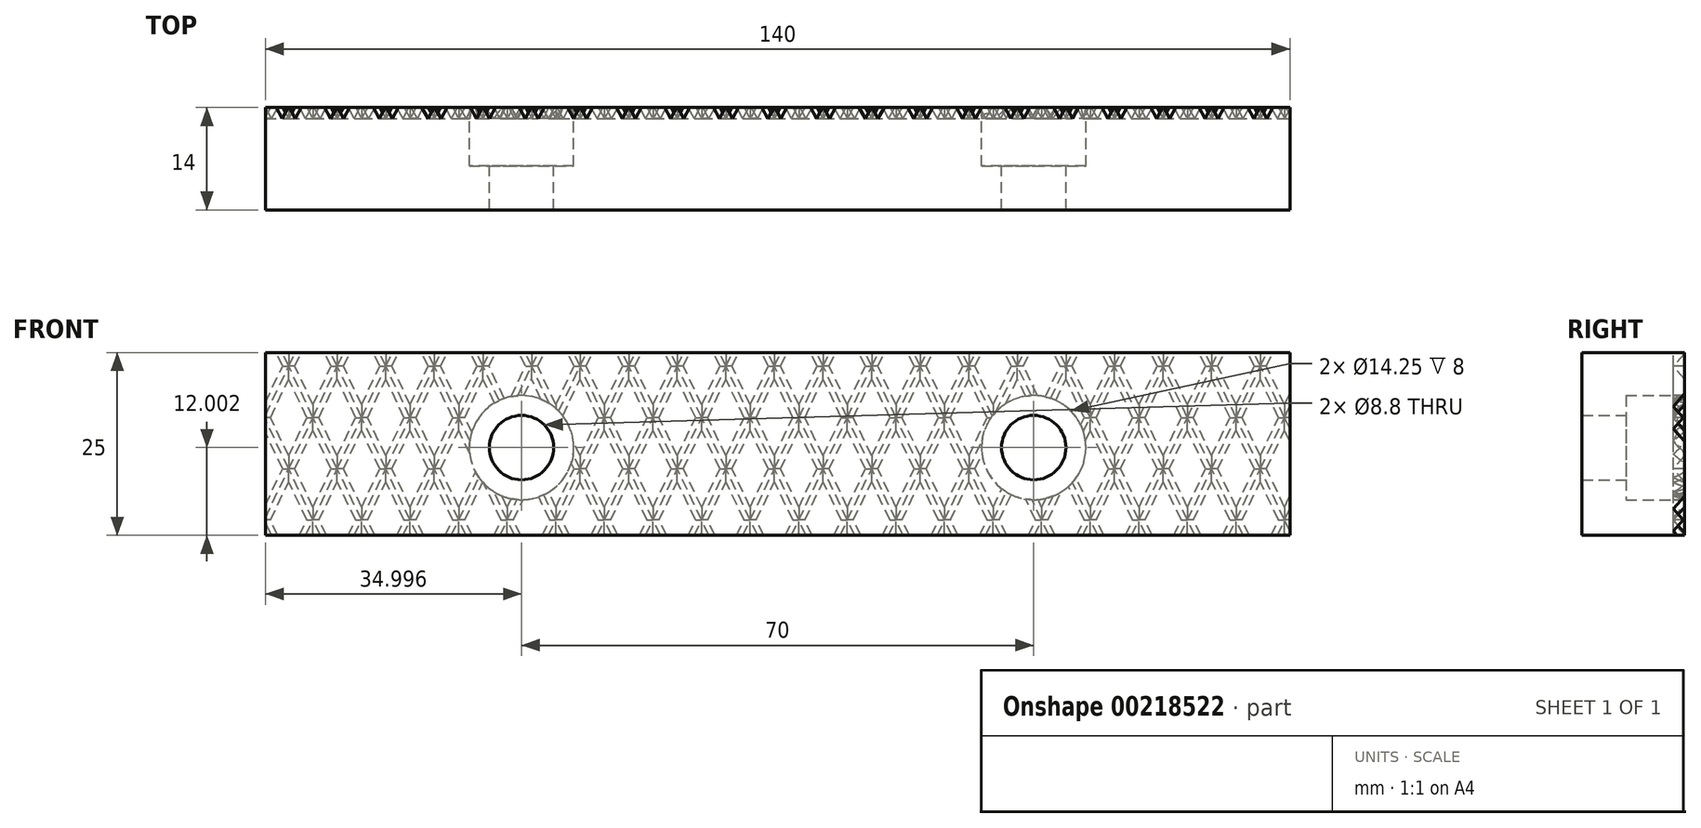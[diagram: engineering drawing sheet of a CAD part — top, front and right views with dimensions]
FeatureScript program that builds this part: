
annotation { "Feature Type Name" : "Feature", "Feature Type Description" : "" }
export const myFeature = defineFeature(function(context is Context, id is Id, definition is map)
    precondition{}
    {
        {
            var Q0;
            Q0=qCreatedBy(makeId("Front.planeOp"),FACE);
            var sketch = newSketch(context, id + "F0", { "sketchPlane" : qUnion([Q0])});
            skLineSegment(sketch, "E0.bottom", {"start": v(-70.74, 11.15) * mm, "end": v(69.26, 11.15) * mm});
            skLineSegment(sketch, "E0.top", {"start": v(-70.74, -13.85) * mm, "end": v(69.26, -13.85) * mm});
            skLineSegment(sketch, "E0.left", {"start": v(-70.74, 11.15) * mm, "end": v(-70.74, -13.85) * mm});
            skLineSegment(sketch, "E0.right", {"start": v(69.26, 11.15) * mm, "end": v(69.26, -13.85) * mm});
            skLineSegment(sketch, "E1", {"start": v(-70.74, -13.85) * mm, "end": v(-35.74, -13.85) * mm});
            skLineSegment(sketch, "E2", {"start": v(-35.74, -13.85) * mm, "end": v(-35.74, -1.85) * mm});
            skLineSegment(sketch, "E3", {"start": v(-35.74, -1.85) * mm, "end": v(34.26, -1.85) * mm});
            skSolve(sketch);
        }
        {
            var Q0;
            Q0=makeQuery(id+"F0.imprint","IMPRINT",FACE,{"disambiguationData":[TD([[makeQuery(id+"F0.imprint","IMPRINT",EDGE,{"derivedFrom":sQuery(id+"F0.wireOp",EDGE,"E0.bottom")}),-1.0]])]});
            extrude(context, id + "F1", {"entities" : qUnion([Q0]), "depth" : 14 * mm});
        }
        {
            var Q0;
            Q0=sQuery(id+"F0.wireOp",VERTEX,"E3.start");
            var Q1;
            Q1=sQuery(id+"F0.wireOp",VERTEX,"E3.end");
            var Q2;
            Q2=makeQuery(id+"F1.opExtrude","SWEPT_BODY",BODY,{"disambiguationData":[OSD([sQuery(id+"F0.wireOp",EDGE,"E0.bottom"),sQuery(id+"F0.wireOp",EDGE,"E0.top"),sQuery(id+"F0.wireOp",EDGE,"E0.left"),sQuery(id+"F0.wireOp",EDGE,"E0.right"),sQuery(id+"F0.wireOp",EDGE,"E1")])]});
            hole(context, id + "F2", {"style" : HoleStyle.C_BORE, "endStyle" : HoleEndStyle.THROUGH, "oppositeDirection" : true, "standardTappedOrClearance" : lookupTablePath({ "standard" : "ISO", "fit" : "Normal", "size" : "M8", "type" : "Clearance" }), "standardBlindInLast" : lookupTablePath({ "fit" : "Standard", "standard" : "ISO", "size" : "M8", "type" : "Clearance" }), "holeDiameter" : 8.8 * mm, "cBoreDiameter" : 14.25 * mm, "cBoreDepth" : 8 * mm, "isTappedThrough" : true, "tappedDepth" : 12 * mm, "tapClearance" : 3, "locations" : qUnion([Q0, Q1]), "scope" : qUnion([Q2])});
        }
        {
            var Q0;
            Q0=sQuery(id+"F0.wireOp",EDGE,"E0.top");
            cPoint(context, id + "F3", {"entities" : qUnion([Q0]), "parameter" : 0.5});
        }
        {
            var Q0;
            Q0=makeQuery(id+"F1.opExtrude","SWEPT_EDGE",EDGE,{"disambiguationData":[OSD([sQuery(id+"F0.wireOp",EDGE,"E0.bottom"),sQuery(id+"F0.wireOp",EDGE,"E0.right")])]});
            var Q1;
            Q1 = qCreatedBy(id + "F3" ,VERTEX);
            cPlane(context, id + "F4", {"entities" : qUnion([Q0, Q1]), "cplaneType" : CPlaneType.LINE_ANGLE, "offset" : 25 * mm, "angle" : 45 * degree, "width" : 150 * mm, "height" : 150 * mm});
        }
        {
            var Q0;
            Q0=qCreatedBy(id+"F4.planeOp",FACE);
            var sketch = newSketch(context, id + "F5", { "sketchPlane" : qUnion([Q0])});
            skLineSegment(sketch, "E4", {"start": v(0, 0) * mm, "end": v(126.29, 0) * mm});
            skLineSegment(sketch, "E5", {"start": v(0, 0) * mm, "end": v(-124.5, 0) * mm});
            skLineSegment(sketch, "E6", {"start": v(67.71, 0) * mm, "end": v(66.21, 0) * mm});
            skLineSegment(sketch, "E7", {"start": v(66.96, -1.5) * mm, "end": v(66.21, 0) * mm});
            skLineSegment(sketch, "E8", {"start": v(66.96, -1.5) * mm, "end": v(67.71, 0) * mm});
            skLineSegment(sketch, "E9.1.0.0", {"start": v(60.96, -1.5) * mm, "end": v(60.21, 0) * mm});
            skLineSegment(sketch, "E9.2.0.0", {"start": v(54.96, -1.5) * mm, "end": v(54.21, 0) * mm});
            skLineSegment(sketch, "E9.3.0.0", {"start": v(48.96, -1.5) * mm, "end": v(48.21, 0) * mm});
            skLineSegment(sketch, "E9.4.0.0", {"start": v(42.96, -1.5) * mm, "end": v(42.21, 0) * mm});
            skLineSegment(sketch, "E9.5.0.0", {"start": v(36.96, -1.5) * mm, "end": v(36.21, 0) * mm});
            skLineSegment(sketch, "E9.6.0.0", {"start": v(30.96, -1.5) * mm, "end": v(30.21, 0) * mm});
            skLineSegment(sketch, "E9.7.0.0", {"start": v(24.96, -1.5) * mm, "end": v(24.21, 0) * mm});
            skLineSegment(sketch, "E9.8.0.0", {"start": v(18.96, -1.5) * mm, "end": v(18.21, 0) * mm});
            skLineSegment(sketch, "E9.9.0.0", {"start": v(12.96, -1.5) * mm, "end": v(12.21, 0) * mm});
            skLineSegment(sketch, "E9.10.0.0", {"start": v(6.96, -1.5) * mm, "end": v(6.21, 0) * mm});
            skLineSegment(sketch, "E9.11.0.0", {"start": v(0.96, -1.5) * mm, "end": v(0.21, 0) * mm});
            skLineSegment(sketch, "E9.12.0.0", {"start": v(-5.04, -1.5) * mm, "end": v(-5.79, 0) * mm});
            skLineSegment(sketch, "E9.13.0.0", {"start": v(-11.04, -1.5) * mm, "end": v(-11.79, 0) * mm});
            skLineSegment(sketch, "E9.14.0.0", {"start": v(-17.04, -1.5) * mm, "end": v(-17.79, 0) * mm});
            skLineSegment(sketch, "E9.15.0.0", {"start": v(-23.04, -1.5) * mm, "end": v(-23.79, 0) * mm});
            skLineSegment(sketch, "E9.16.0.0", {"start": v(-29.04, -1.5) * mm, "end": v(-29.79, 0) * mm});
            skLineSegment(sketch, "E9.17.0.0", {"start": v(-35.04, -1.5) * mm, "end": v(-35.79, 0) * mm});
            skLineSegment(sketch, "E9.18.0.0", {"start": v(-41.04, -1.5) * mm, "end": v(-41.79, 0) * mm});
            skLineSegment(sketch, "E9.19.0.0", {"start": v(-47.04, -1.5) * mm, "end": v(-47.79, 0) * mm});
            skLineSegment(sketch, "E9.20.0.0", {"start": v(-53.04, -1.5) * mm, "end": v(-53.79, 0) * mm});
            skLineSegment(sketch, "E9.21.0.0", {"start": v(-59.04, -1.5) * mm, "end": v(-59.79, 0) * mm});
            skLineSegment(sketch, "E9.22.0.0", {"start": v(-65.04, -1.5) * mm, "end": v(-65.79, 0) * mm});
            skLineSegment(sketch, "E9.23.0.0", {"start": v(-71.04, -1.5) * mm, "end": v(-71.79, 0) * mm});
            skLineSegment(sketch, "E9.24.0.0", {"start": v(-77.04, -1.5) * mm, "end": v(-77.79, 0) * mm});
            skLineSegment(sketch, "E9.25.0.0", {"start": v(-83.04, -1.5) * mm, "end": v(-83.79, 0) * mm});
            skLineSegment(sketch, "E9.26.0.0", {"start": v(-89.04, -1.5) * mm, "end": v(-89.79, 0) * mm});
            skLineSegment(sketch, "E9.27.0.0", {"start": v(-95.04, -1.5) * mm, "end": v(-95.79, 0) * mm});
            skLineSegment(sketch, "E9.28.0.0", {"start": v(-101.04, -1.5) * mm, "end": v(-101.79, 0) * mm});
            skLineSegment(sketch, "E9.29.0.0", {"start": v(-107.04, -1.5) * mm, "end": v(-107.79, 0) * mm});
            skLineSegment(sketch, "E9.direction1", {"start": v(66.96, -1.5) * mm, "end": v(60.96, -1.5) * mm, "construction": true});
            skLineSegment(sketch, "E10.1.0.0", {"start": v(60.96, -1.5) * mm, "end": v(61.71, 0) * mm});
            skLineSegment(sketch, "E10.2.0.0", {"start": v(54.96, -1.5) * mm, "end": v(55.71, 0) * mm});
            skLineSegment(sketch, "E10.3.0.0", {"start": v(48.96, -1.5) * mm, "end": v(49.71, 0) * mm});
            skLineSegment(sketch, "E10.4.0.0", {"start": v(42.96, -1.5) * mm, "end": v(43.71, 0) * mm});
            skLineSegment(sketch, "E10.5.0.0", {"start": v(36.96, -1.5) * mm, "end": v(37.71, 0) * mm});
            skLineSegment(sketch, "E10.6.0.0", {"start": v(30.96, -1.5) * mm, "end": v(31.71, 0) * mm});
            skLineSegment(sketch, "E10.7.0.0", {"start": v(24.96, -1.5) * mm, "end": v(25.71, 0) * mm});
            skLineSegment(sketch, "E10.8.0.0", {"start": v(18.96, -1.5) * mm, "end": v(19.71, 0) * mm});
            skLineSegment(sketch, "E10.9.0.0", {"start": v(12.96, -1.5) * mm, "end": v(13.71, 0) * mm});
            skLineSegment(sketch, "E10.10.0.0", {"start": v(6.96, -1.5) * mm, "end": v(7.71, 0) * mm});
            skLineSegment(sketch, "E10.11.0.0", {"start": v(0.96, -1.5) * mm, "end": v(1.71, 0) * mm});
            skLineSegment(sketch, "E10.12.0.0", {"start": v(-5.04, -1.5) * mm, "end": v(-4.29, 0) * mm});
            skLineSegment(sketch, "E10.13.0.0", {"start": v(-11.04, -1.5) * mm, "end": v(-10.29, 0) * mm});
            skLineSegment(sketch, "E10.14.0.0", {"start": v(-17.04, -1.5) * mm, "end": v(-16.29, 0) * mm});
            skLineSegment(sketch, "E10.15.0.0", {"start": v(-23.04, -1.5) * mm, "end": v(-22.29, 0) * mm});
            skLineSegment(sketch, "E10.16.0.0", {"start": v(-29.04, -1.5) * mm, "end": v(-28.29, 0) * mm});
            skLineSegment(sketch, "E10.17.0.0", {"start": v(-35.04, -1.5) * mm, "end": v(-34.29, 0) * mm});
            skLineSegment(sketch, "E10.18.0.0", {"start": v(-41.04, -1.5) * mm, "end": v(-40.29, 0) * mm});
            skLineSegment(sketch, "E10.19.0.0", {"start": v(-47.04, -1.5) * mm, "end": v(-46.29, 0) * mm});
            skLineSegment(sketch, "E10.20.0.0", {"start": v(-53.04, -1.5) * mm, "end": v(-52.29, 0) * mm});
            skLineSegment(sketch, "E10.21.0.0", {"start": v(-59.04, -1.5) * mm, "end": v(-58.29, 0) * mm});
            skLineSegment(sketch, "E10.22.0.0", {"start": v(-65.04, -1.5) * mm, "end": v(-64.29, 0) * mm});
            skLineSegment(sketch, "E10.23.0.0", {"start": v(-71.04, -1.5) * mm, "end": v(-70.29, 0) * mm});
            skLineSegment(sketch, "E10.24.0.0", {"start": v(-77.04, -1.5) * mm, "end": v(-76.29, 0) * mm});
            skLineSegment(sketch, "E10.25.0.0", {"start": v(-83.04, -1.5) * mm, "end": v(-82.29, 0) * mm});
            skLineSegment(sketch, "E10.26.0.0", {"start": v(-89.04, -1.5) * mm, "end": v(-88.29, 0) * mm});
            skLineSegment(sketch, "E10.27.0.0", {"start": v(-95.04, -1.5) * mm, "end": v(-94.29, 0) * mm});
            skLineSegment(sketch, "E10.28.0.0", {"start": v(-101.04, -1.5) * mm, "end": v(-100.29, 0) * mm});
            skLineSegment(sketch, "E10.29.0.0", {"start": v(-107.04, -1.5) * mm, "end": v(-106.29, 0) * mm});
            skLineSegment(sketch, "E11.1.0.0", {"start": v(61.71, 0) * mm, "end": v(60.21, 0) * mm});
            skLineSegment(sketch, "E11.2.0.0", {"start": v(55.71, 0) * mm, "end": v(54.21, 0) * mm});
            skLineSegment(sketch, "E11.3.0.0", {"start": v(49.71, 0) * mm, "end": v(48.21, 0) * mm});
            skLineSegment(sketch, "E11.4.0.0", {"start": v(43.71, 0) * mm, "end": v(42.21, 0) * mm});
            skLineSegment(sketch, "E11.5.0.0", {"start": v(37.71, 0) * mm, "end": v(36.21, 0) * mm});
            skLineSegment(sketch, "E11.6.0.0", {"start": v(31.71, 0) * mm, "end": v(30.21, 0) * mm});
            skLineSegment(sketch, "E11.7.0.0", {"start": v(25.71, 0) * mm, "end": v(24.21, 0) * mm});
            skLineSegment(sketch, "E11.8.0.0", {"start": v(19.71, 0) * mm, "end": v(18.21, 0) * mm});
            skLineSegment(sketch, "E11.9.0.0", {"start": v(13.71, 0) * mm, "end": v(12.21, 0) * mm});
            skLineSegment(sketch, "E11.10.0.0", {"start": v(7.71, 0) * mm, "end": v(6.21, 0) * mm});
            skLineSegment(sketch, "E11.11.0.0", {"start": v(1.71, 0) * mm, "end": v(0.21, 0) * mm});
            skLineSegment(sketch, "E11.12.0.0", {"start": v(-4.29, 0) * mm, "end": v(-5.79, 0) * mm});
            skLineSegment(sketch, "E11.13.0.0", {"start": v(-10.29, 0) * mm, "end": v(-11.79, 0) * mm});
            skLineSegment(sketch, "E11.14.0.0", {"start": v(-16.29, 0) * mm, "end": v(-17.79, 0) * mm});
            skLineSegment(sketch, "E11.15.0.0", {"start": v(-22.29, 0) * mm, "end": v(-23.79, 0) * mm});
            skLineSegment(sketch, "E11.16.0.0", {"start": v(-28.29, 0) * mm, "end": v(-29.79, 0) * mm});
            skLineSegment(sketch, "E11.17.0.0", {"start": v(-34.29, 0) * mm, "end": v(-35.79, 0) * mm});
            skLineSegment(sketch, "E11.18.0.0", {"start": v(-40.29, 0) * mm, "end": v(-41.79, 0) * mm});
            skLineSegment(sketch, "E11.19.0.0", {"start": v(-46.29, 0) * mm, "end": v(-47.79, 0) * mm});
            skLineSegment(sketch, "E11.20.0.0", {"start": v(-52.29, 0) * mm, "end": v(-53.79, 0) * mm});
            skLineSegment(sketch, "E11.21.0.0", {"start": v(-58.29, 0) * mm, "end": v(-59.79, 0) * mm});
            skLineSegment(sketch, "E11.22.0.0", {"start": v(-64.29, 0) * mm, "end": v(-65.79, 0) * mm});
            skLineSegment(sketch, "E11.23.0.0", {"start": v(-70.29, 0) * mm, "end": v(-71.79, 0) * mm});
            skLineSegment(sketch, "E11.24.0.0", {"start": v(-76.29, 0) * mm, "end": v(-77.79, 0) * mm});
            skLineSegment(sketch, "E11.25.0.0", {"start": v(-82.29, 0) * mm, "end": v(-83.79, 0) * mm});
            skLineSegment(sketch, "E11.26.0.0", {"start": v(-88.29, 0) * mm, "end": v(-89.79, 0) * mm});
            skLineSegment(sketch, "E11.27.0.0", {"start": v(-94.29, 0) * mm, "end": v(-95.79, 0) * mm});
            skLineSegment(sketch, "E11.28.0.0", {"start": v(-100.29, 0) * mm, "end": v(-101.79, 0) * mm});
            skLineSegment(sketch, "E11.29.0.0", {"start": v(-106.29, 0) * mm, "end": v(-107.79, 0) * mm});
            skLineSegment(sketch, "E11.direction1", {"start": v(66.21, 0) * mm, "end": v(60.21, 0) * mm, "construction": true});
            skSolve(sketch);
        }
        {
            var Q0;
            Q0 = qSketchRegion(id + "F5", true);
            extrude(context, id + "F6", {"entities" : qUnion([Q0]), "operationType" : NewBodyOperationType.REMOVE, "endBound" : BoundingType.SYMMETRIC, "oppositeDirection" : true, "depth" : 300 * mm});
        }
        {
            var Q0;
            Q0=sQuery(id+"F0.wireOp",EDGE,"E0.top");
            cPoint(context, id + "F7", {"entities" : qUnion([Q0]), "parameter" : 0.5});
        }
        {
            var Q0;
            Q0=makeQuery(id+"F1.opExtrude","SWEPT_EDGE",EDGE,{"disambiguationData":[OSD([sQuery(id+"F0.wireOp",EDGE,"E0.bottom"),sQuery(id+"F0.wireOp",EDGE,"E0.left")])]});
            var Q1;
            Q1 = qCreatedBy(id + "F7" ,VERTEX);
            cPlane(context, id + "F8", {"entities" : qUnion([Q0, Q1]), "cplaneType" : CPlaneType.LINE_ANGLE, "offset" : 25 * mm, "angle" : 135 * degree, "width" : 150 * mm, "height" : 150 * mm});
        }
        {
            var Q0;
            Q0=qCreatedBy(id+"F8.planeOp",FACE);
            var sketch = newSketch(context, id + "F9", { "sketchPlane" : qUnion([Q0])});
            skLineSegment(sketch, "E12", {"start": v(0, 0) * mm, "end": v(-89.04, 0) * mm});
            skLineSegment(sketch, "E13", {"start": v(0, 0) * mm, "end": v(96.12, 0) * mm});
            skLineSegment(sketch, "E14", {"start": v(-69.84, 0) * mm, "end": v(-68.34, 0) * mm});
            skLineSegment(sketch, "E15", {"start": v(-69.1, -1.5) * mm, "end": v(-68.34, 0) * mm});
            skLineSegment(sketch, "E16", {"start": v(-69.1, -1.5) * mm, "end": v(-69.84, 0) * mm});
            skLineSegment(sketch, "E17.1.0.0", {"start": v(-63.1, -1.5) * mm, "end": v(-63.84, 0) * mm});
            skLineSegment(sketch, "E17.2.0.0", {"start": v(-57.1, -1.5) * mm, "end": v(-57.84, 0) * mm});
            skLineSegment(sketch, "E17.3.0.0", {"start": v(-51.1, -1.5) * mm, "end": v(-51.84, 0) * mm});
            skLineSegment(sketch, "E17.4.0.0", {"start": v(-45.1, -1.5) * mm, "end": v(-45.84, 0) * mm});
            skLineSegment(sketch, "E17.5.0.0", {"start": v(-39.1, -1.5) * mm, "end": v(-39.84, 0) * mm});
            skLineSegment(sketch, "E17.6.0.0", {"start": v(-33.1, -1.5) * mm, "end": v(-33.84, 0) * mm});
            skLineSegment(sketch, "E17.7.0.0", {"start": v(-27.1, -1.5) * mm, "end": v(-27.84, 0) * mm});
            skLineSegment(sketch, "E17.8.0.0", {"start": v(-21.1, -1.5) * mm, "end": v(-21.84, 0) * mm});
            skLineSegment(sketch, "E17.9.0.0", {"start": v(-15.1, -1.5) * mm, "end": v(-15.84, 0) * mm});
            skLineSegment(sketch, "E17.10.0.0", {"start": v(-9.1, -1.5) * mm, "end": v(-9.84, 0) * mm});
            skLineSegment(sketch, "E17.11.0.0", {"start": v(-3.1, -1.5) * mm, "end": v(-3.84, 0) * mm});
            skLineSegment(sketch, "E17.12.0.0", {"start": v(2.9, -1.5) * mm, "end": v(2.16, 0) * mm});
            skLineSegment(sketch, "E17.13.0.0", {"start": v(8.9, -1.5) * mm, "end": v(8.16, 0) * mm});
            skLineSegment(sketch, "E17.14.0.0", {"start": v(14.9, -1.5) * mm, "end": v(14.16, 0) * mm});
            skLineSegment(sketch, "E17.15.0.0", {"start": v(20.9, -1.5) * mm, "end": v(20.16, 0) * mm});
            skLineSegment(sketch, "E17.16.0.0", {"start": v(26.9, -1.5) * mm, "end": v(26.16, 0) * mm});
            skLineSegment(sketch, "E17.17.0.0", {"start": v(32.9, -1.5) * mm, "end": v(32.16, 0) * mm});
            skLineSegment(sketch, "E17.18.0.0", {"start": v(38.9, -1.5) * mm, "end": v(38.16, 0) * mm});
            skLineSegment(sketch, "E17.19.0.0", {"start": v(44.9, -1.5) * mm, "end": v(44.16, 0) * mm});
            skLineSegment(sketch, "E17.20.0.0", {"start": v(50.9, -1.5) * mm, "end": v(50.16, 0) * mm});
            skLineSegment(sketch, "E17.21.0.0", {"start": v(56.9, -1.5) * mm, "end": v(56.16, 0) * mm});
            skLineSegment(sketch, "E17.22.0.0", {"start": v(62.9, -1.5) * mm, "end": v(62.16, 0) * mm});
            skLineSegment(sketch, "E17.23.0.0", {"start": v(68.9, -1.5) * mm, "end": v(68.16, 0) * mm});
            skLineSegment(sketch, "E17.24.0.0", {"start": v(74.9, -1.5) * mm, "end": v(74.16, 0) * mm});
            skLineSegment(sketch, "E17.25.0.0", {"start": v(80.9, -1.5) * mm, "end": v(80.16, 0) * mm});
            skLineSegment(sketch, "E17.26.0.0", {"start": v(86.9, -1.5) * mm, "end": v(86.16, 0) * mm});
            skLineSegment(sketch, "E17.27.0.0", {"start": v(92.9, -1.5) * mm, "end": v(92.16, 0) * mm});
            skLineSegment(sketch, "E17.28.0.0", {"start": v(98.9, -1.5) * mm, "end": v(98.16, 0) * mm});
            skLineSegment(sketch, "E17.29.0.0", {"start": v(104.9, -1.5) * mm, "end": v(104.16, 0) * mm});
            skLineSegment(sketch, "E17.direction1", {"start": v(-69.1, -1.5) * mm, "end": v(-63.1, -1.5) * mm, "construction": true});
            skLineSegment(sketch, "E18.1.0.0", {"start": v(-63.1, -1.5) * mm, "end": v(-62.34, 0) * mm});
            skLineSegment(sketch, "E18.2.0.0", {"start": v(-57.1, -1.5) * mm, "end": v(-56.34, 0) * mm});
            skLineSegment(sketch, "E18.3.0.0", {"start": v(-51.1, -1.5) * mm, "end": v(-50.34, 0) * mm});
            skLineSegment(sketch, "E18.4.0.0", {"start": v(-45.1, -1.5) * mm, "end": v(-44.34, 0) * mm});
            skLineSegment(sketch, "E18.5.0.0", {"start": v(-39.1, -1.5) * mm, "end": v(-38.34, 0) * mm});
            skLineSegment(sketch, "E18.6.0.0", {"start": v(-33.1, -1.5) * mm, "end": v(-32.34, 0) * mm});
            skLineSegment(sketch, "E18.7.0.0", {"start": v(-27.1, -1.5) * mm, "end": v(-26.34, 0) * mm});
            skLineSegment(sketch, "E18.8.0.0", {"start": v(-21.1, -1.5) * mm, "end": v(-20.34, 0) * mm});
            skLineSegment(sketch, "E18.9.0.0", {"start": v(-15.1, -1.5) * mm, "end": v(-14.34, 0) * mm});
            skLineSegment(sketch, "E18.10.0.0", {"start": v(-9.1, -1.5) * mm, "end": v(-8.34, 0) * mm});
            skLineSegment(sketch, "E18.11.0.0", {"start": v(-3.1, -1.5) * mm, "end": v(-2.34, 0) * mm});
            skLineSegment(sketch, "E18.12.0.0", {"start": v(2.9, -1.5) * mm, "end": v(3.66, 0) * mm});
            skLineSegment(sketch, "E18.13.0.0", {"start": v(8.9, -1.5) * mm, "end": v(9.66, 0) * mm});
            skLineSegment(sketch, "E18.14.0.0", {"start": v(14.9, -1.5) * mm, "end": v(15.66, 0) * mm});
            skLineSegment(sketch, "E18.15.0.0", {"start": v(20.9, -1.5) * mm, "end": v(21.66, 0) * mm});
            skLineSegment(sketch, "E18.16.0.0", {"start": v(26.9, -1.5) * mm, "end": v(27.66, 0) * mm});
            skLineSegment(sketch, "E18.17.0.0", {"start": v(32.9, -1.5) * mm, "end": v(33.66, 0) * mm});
            skLineSegment(sketch, "E18.18.0.0", {"start": v(38.9, -1.5) * mm, "end": v(39.66, 0) * mm});
            skLineSegment(sketch, "E18.19.0.0", {"start": v(44.9, -1.5) * mm, "end": v(45.66, 0) * mm});
            skLineSegment(sketch, "E18.20.0.0", {"start": v(50.9, -1.5) * mm, "end": v(51.66, 0) * mm});
            skLineSegment(sketch, "E18.21.0.0", {"start": v(56.9, -1.5) * mm, "end": v(57.66, 0) * mm});
            skLineSegment(sketch, "E18.22.0.0", {"start": v(62.9, -1.5) * mm, "end": v(63.66, 0) * mm});
            skLineSegment(sketch, "E18.23.0.0", {"start": v(68.9, -1.5) * mm, "end": v(69.66, 0) * mm});
            skLineSegment(sketch, "E18.24.0.0", {"start": v(74.9, -1.5) * mm, "end": v(75.66, 0) * mm});
            skLineSegment(sketch, "E18.25.0.0", {"start": v(80.9, -1.5) * mm, "end": v(81.66, 0) * mm});
            skLineSegment(sketch, "E18.26.0.0", {"start": v(86.9, -1.5) * mm, "end": v(87.66, 0) * mm});
            skLineSegment(sketch, "E18.27.0.0", {"start": v(92.9, -1.5) * mm, "end": v(93.66, 0) * mm});
            skLineSegment(sketch, "E18.28.0.0", {"start": v(98.9, -1.5) * mm, "end": v(99.66, 0) * mm});
            skLineSegment(sketch, "E18.29.0.0", {"start": v(104.9, -1.5) * mm, "end": v(105.66, 0) * mm});
            skLineSegment(sketch, "E19.1.0.0", {"start": v(-63.84, 0) * mm, "end": v(-62.34, 0) * mm});
            skLineSegment(sketch, "E19.2.0.0", {"start": v(-57.84, 0) * mm, "end": v(-56.34, 0) * mm});
            skLineSegment(sketch, "E19.3.0.0", {"start": v(-51.84, 0) * mm, "end": v(-50.34, 0) * mm});
            skLineSegment(sketch, "E19.4.0.0", {"start": v(-45.84, 0) * mm, "end": v(-44.34, 0) * mm});
            skLineSegment(sketch, "E19.5.0.0", {"start": v(-39.84, 0) * mm, "end": v(-38.34, 0) * mm});
            skLineSegment(sketch, "E19.6.0.0", {"start": v(-33.84, 0) * mm, "end": v(-32.34, 0) * mm});
            skLineSegment(sketch, "E19.7.0.0", {"start": v(-27.84, 0) * mm, "end": v(-26.34, 0) * mm});
            skLineSegment(sketch, "E19.8.0.0", {"start": v(-21.84, 0) * mm, "end": v(-20.34, 0) * mm});
            skLineSegment(sketch, "E19.9.0.0", {"start": v(-15.84, 0) * mm, "end": v(-14.34, 0) * mm});
            skLineSegment(sketch, "E19.10.0.0", {"start": v(-9.84, 0) * mm, "end": v(-8.34, 0) * mm});
            skLineSegment(sketch, "E19.11.0.0", {"start": v(-3.84, 0) * mm, "end": v(-2.34, 0) * mm});
            skLineSegment(sketch, "E19.12.0.0", {"start": v(2.16, 0) * mm, "end": v(3.66, 0) * mm});
            skLineSegment(sketch, "E19.13.0.0", {"start": v(8.16, 0) * mm, "end": v(9.66, 0) * mm});
            skLineSegment(sketch, "E19.14.0.0", {"start": v(14.16, 0) * mm, "end": v(15.66, 0) * mm});
            skLineSegment(sketch, "E19.15.0.0", {"start": v(20.16, 0) * mm, "end": v(21.66, 0) * mm});
            skLineSegment(sketch, "E19.16.0.0", {"start": v(26.16, 0) * mm, "end": v(27.66, 0) * mm});
            skLineSegment(sketch, "E19.17.0.0", {"start": v(32.16, 0) * mm, "end": v(33.66, 0) * mm});
            skLineSegment(sketch, "E19.18.0.0", {"start": v(38.16, 0) * mm, "end": v(39.66, 0) * mm});
            skLineSegment(sketch, "E19.19.0.0", {"start": v(44.16, 0) * mm, "end": v(45.66, 0) * mm});
            skLineSegment(sketch, "E19.20.0.0", {"start": v(50.16, 0) * mm, "end": v(51.66, 0) * mm});
            skLineSegment(sketch, "E19.21.0.0", {"start": v(56.16, 0) * mm, "end": v(57.66, 0) * mm});
            skLineSegment(sketch, "E19.22.0.0", {"start": v(62.16, 0) * mm, "end": v(63.66, 0) * mm});
            skLineSegment(sketch, "E19.23.0.0", {"start": v(68.16, 0) * mm, "end": v(69.66, 0) * mm});
            skLineSegment(sketch, "E19.24.0.0", {"start": v(74.16, 0) * mm, "end": v(75.66, 0) * mm});
            skLineSegment(sketch, "E19.25.0.0", {"start": v(80.16, 0) * mm, "end": v(81.66, 0) * mm});
            skLineSegment(sketch, "E19.26.0.0", {"start": v(86.16, 0) * mm, "end": v(87.66, 0) * mm});
            skLineSegment(sketch, "E19.27.0.0", {"start": v(92.16, 0) * mm, "end": v(93.66, 0) * mm});
            skLineSegment(sketch, "E19.28.0.0", {"start": v(98.16, 0) * mm, "end": v(99.66, 0) * mm});
            skLineSegment(sketch, "E19.29.0.0", {"start": v(104.16, 0) * mm, "end": v(105.66, 0) * mm});
            skLineSegment(sketch, "E19.direction1", {"start": v(-69.84, 0) * mm, "end": v(-63.84, 0) * mm, "construction": true});
            skSolve(sketch);
        }
        {
            var Q0;
            Q0 = qSketchRegion(id + "F9", true);
            extrude(context, id + "F10", {"entities" : qUnion([Q0]), "operationType" : NewBodyOperationType.REMOVE, "endBound" : BoundingType.SYMMETRIC, "oppositeDirection" : true, "depth" : 300 * mm});
        }
    });
